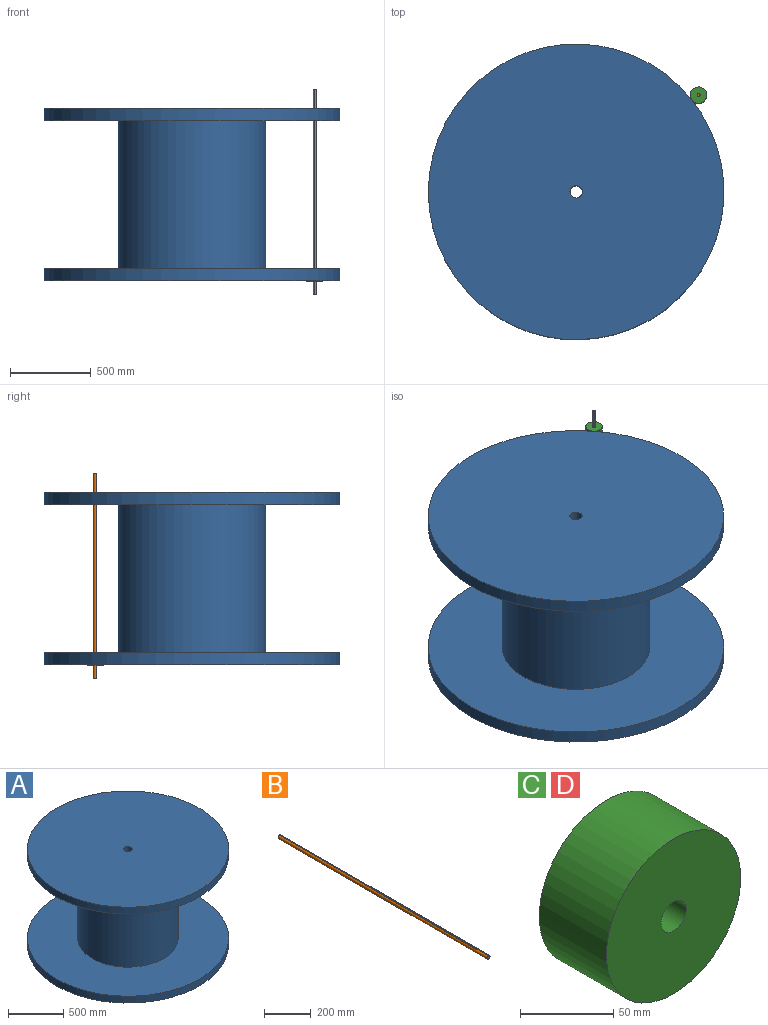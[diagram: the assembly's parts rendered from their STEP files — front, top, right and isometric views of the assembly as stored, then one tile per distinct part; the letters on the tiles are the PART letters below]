
ASSEMBLY  parts=4 mates=3
PART A: 12 faces, bbox 1828.8x1828.8x1066.8 mm
  f0: plane 1828.8x1828.8mm, normal (0,0,1), area 2622211.2mm2, adj f1,f11
  f1: cylinder r=38.1mm len=76.2mm, axis (0,0,-1), area 18241.5mm2, adj f0,f2
  f2: plane 812.8x812.8mm, normal (0,0,-1), area 514308.1mm2, adj f1,f3
  f3: cylinder r=406.4mm len=914.4mm, axis (0,0,-1), area 2334908.1mm2, adj f2,f4
  f4: plane 812.8x812.8mm, normal (0,0,1), area 514308.1mm2, adj f3,f5
  f5: cylinder r=38.1mm len=76.2mm, axis (0,0,-1), area 18241.5mm2, adj f4,f6
  f6: plane 1828.8x1828.8mm, normal (0,0,-1), area 2622211.2mm2, adj f5,f7
  f7: cylinder r=914.4mm len=1828.8mm, axis (0,0,-1), area 437795.3mm2, adj f6,f8
  f8: plane 1828.8x1828.8mm, normal (0,0,1), area 1970078.7mm2, adj f7,f9
  f9: cylinder r=457.2mm len=914.4mm, axis (0,0,-1), area 2626771.6mm2, adj f8,f10
  f10: plane 1828.8x1828.8mm, normal (0,0,-1), area 1970078.7mm2, adj f9,f11
  f11: cylinder r=914.4mm len=1828.8mm, axis (0,0,-1), area 437795.3mm2, adj f0,f10
PART B: 6 faces, bbox 19.1x1270x18.7 mm
  f0: plane 1270x2.08mm, normal (1,0,0), area 2640.1mm2, adj f1,f3,f4,f5
  f1: cylinder r=9.53mm len=1270mm, axis (0,1,0), area 69892.9mm2, adj f0,f2,f4,f5
  f2: plane 1270x2.08mm, normal (-1,0,0), area 2640.1mm2, adj f1,f3,f4,f5
  f3: plane 1270x4.76mm, normal (0,0,1), area 6048.4mm2, adj f0,f2,f4,f5
  f4: plane 19.05x18.75mm, normal (0,-1,0), area 274.2mm2, adj f0,f1,f2,f3
  f5: plane 19.05x18.75mm, normal (0,1,0), area 274.2mm2, adj f0,f1,f2,f3
PART C: 4 faces, bbox 101.6x50.8x101.6 mm
  f0: cylinder r=9.53mm len=50.8mm, axis (0,1,0), area 3040.2mm2, adj f2,f3
  f1: cylinder r=50.8mm len=101.6mm, axis (0,1,0), area 16214.6mm2, adj f2,f3
  f2: plane 101.6x101.6mm, normal (0,-1,0), area 7822.3mm2, adj f0,f1
  f3: plane 101.6x101.6mm, normal (0,1,0), area 7822.3mm2, adj f0,f1
PART D: same geometry as C
PLACE A t=(-965.98,-871.74,172.63)mm
PLACE B rot(axis=(1,0,0),90deg) t=(-1016.27,-273.22,895.37)mm
PLACE C rot(axis=(-1,0,0),90deg) t=(-1016.27,-273.22,726.4)mm
PLACE D rot(axis=(-1,0,0),90deg) t=(-1016.27,-273.22,-296.21)mm
MATE cylindrical D.f1 <-> C.f1  axis (0,0,-1) through (-1016.27,-273.22,-270.81)mm
MATE cylindrical D.f1 <-> B.f1  axis (0,0,-1) through (-1016.27,-273.22,-270.81)mm
MATE parallel D.f1 <-> A.f1  axis (0,0,1) through (-1016.27,-273.22,-245.41)mm
